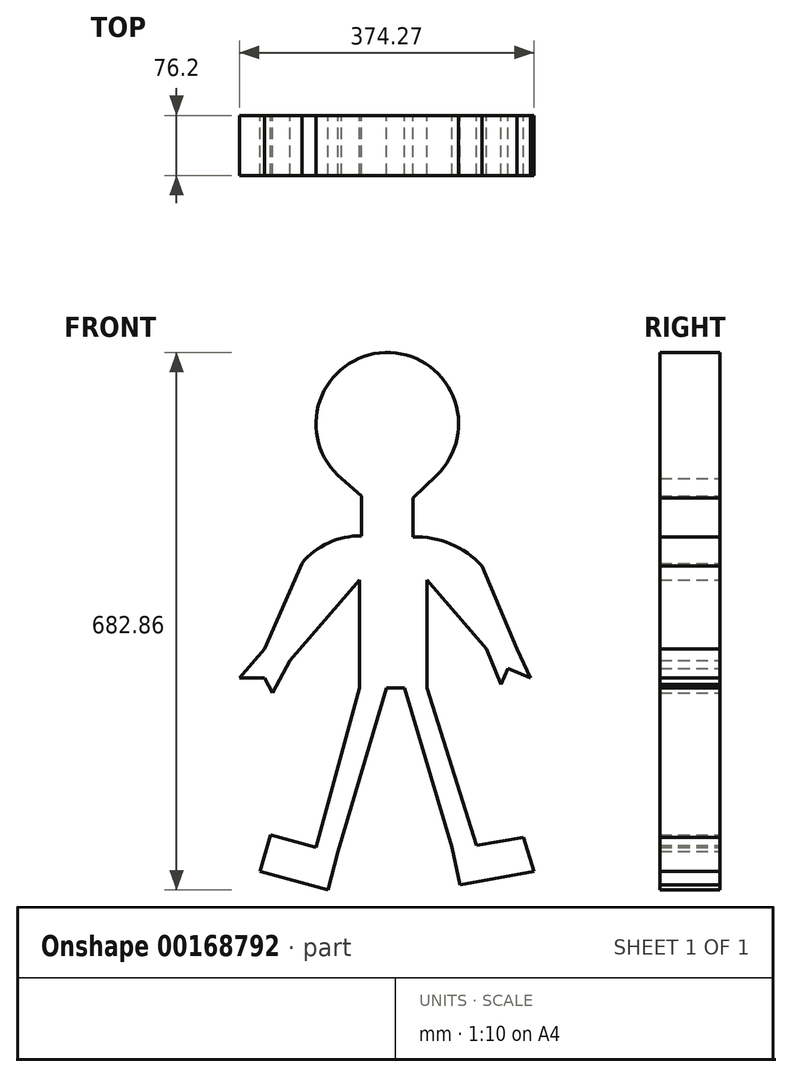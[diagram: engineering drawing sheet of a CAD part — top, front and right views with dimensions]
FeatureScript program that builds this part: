
annotation { "Feature Type Name" : "Feature", "Feature Type Description" : "" }
export const myFeature = defineFeature(function(context is Context, id is Id, definition is map)
    precondition{}
    {
        {
            var Q0;
            Q0=qCreatedBy(makeId("Front.planeOp"),FACE);
            var sketch = newSketch(context, id + "F0", { "sketchPlane" : qUnion([Q0])});
            skLineSegment(sketch, "E0", {"start": v(-65.27, 231.14) * mm, "end": v(-65.27, 180.67) * mm});
            skLineSegment(sketch, "E1", {"start": v(0, 228.8) * mm, "end": v(0, 179.25) * mm});
            skCircle(sketch, "E2", {"center": v(-32.54, 323) * mm, "radius": 90.58 * mm});
            skArc(sketch, "E3", {"start": v(-65.27, 180.67) * mm, "mid": v(-107.07, 171.83) * mm, "end": v(-140.92, 145.77) * mm});
            skArc(sketch, "E4", {"start": v(87.57, 142.42) * mm, "mid": v(47.85, 170.5) * mm, "end": v(0, 179.25) * mm});
            skLineSegment(sketch, "E5", {"start": v(-140.92, 145.77) * mm, "end": v(-188.63, 36.96) * mm});
            skLineSegment(sketch, "E6", {"start": v(-188.63, 36.96) * mm, "end": v(-155.84, 22.59) * mm});
            skLineSegment(sketch, "E7", {"start": v(-155.84, 22.59) * mm, "end": v(-68.1, 124.84) * mm});
            skLineSegment(sketch, "E8", {"start": v(-68.1, 124.84) * mm, "end": v(-68.1, -12.42) * mm});
            skLineSegment(sketch, "E9", {"start": v(-68.1, -12.42) * mm, "end": v(18.1, -12.42) * mm});
            skLineSegment(sketch, "E10", {"start": v(18.1, -12.42) * mm, "end": v(18.1, 124.84) * mm});
            skLineSegment(sketch, "E11", {"start": v(18.1, 124.84) * mm, "end": v(93.49, 36.96) * mm});
            skLineSegment(sketch, "E12", {"start": v(93.49, 36.96) * mm, "end": v(131.93, 36.96) * mm});
            skLineSegment(sketch, "E13", {"start": v(131.93, 36.96) * mm, "end": v(87.57, 142.42) * mm});
            skLineSegment(sketch, "E14", {"start": v(-68.1, -12.42) * mm, "end": v(-123.35, -214.96) * mm});
            skLineSegment(sketch, "E15", {"start": v(-33.79, -12.42) * mm, "end": v(-94.89, -219.99) * mm});
            skLineSegment(sketch, "E16", {"start": v(-10.35, -12.42) * mm, "end": v(49.9, -214.96) * mm});
            skLineSegment(sketch, "E17", {"start": v(18.1, -12.42) * mm, "end": v(80.87, -212.45) * mm});
            skLineSegment(sketch, "E18", {"start": v(80.87, -212.45) * mm, "end": v(140.3, -202.41) * mm});
            skLineSegment(sketch, "E19", {"start": v(140.3, -202.41) * mm, "end": v(153.93, -245.86) * mm});
            skLineSegment(sketch, "E20", {"start": v(153.93, -245.86) * mm, "end": v(59.95, -262.67) * mm});
            skLineSegment(sketch, "E21", {"start": v(59.95, -262.67) * mm, "end": v(49.9, -214.96) * mm});
            skLineSegment(sketch, "E22", {"start": v(-123.35, -214.96) * mm, "end": v(-181.13, -199.2) * mm});
            skLineSegment(sketch, "E23", {"start": v(-181.13, -199.2) * mm, "end": v(-193.86, -245.86) * mm});
            skLineSegment(sketch, "E24", {"start": v(-193.86, -245.86) * mm, "end": v(-107.95, -269.28) * mm});
            skLineSegment(sketch, "E25", {"start": v(-107.95, -269.28) * mm, "end": v(-94.89, -219.99) * mm});
            skLineSegment(sketch, "E26", {"start": v(-188.63, 36.96) * mm, "end": v(-220.34, 0) * mm});
            skLineSegment(sketch, "E27", {"start": v(-220.34, 0) * mm, "end": v(-188.63, 0) * mm});
            skLineSegment(sketch, "E28", {"start": v(-188.63, 0) * mm, "end": v(-178.4, -19.02) * mm});
            skLineSegment(sketch, "E29", {"start": v(-178.4, -19.02) * mm, "end": v(-155.84, 22.59) * mm});
            skLineSegment(sketch, "E30", {"start": v(93.49, 36.96) * mm, "end": v(111.65, -8.12) * mm});
            skLineSegment(sketch, "E31", {"start": v(111.65, -8.12) * mm, "end": v(120.67, 12.45) * mm});
            skLineSegment(sketch, "E32", {"start": v(120.67, 12.45) * mm, "end": v(149.07, 0) * mm});
            skLineSegment(sketch, "E33", {"start": v(149.07, 0) * mm, "end": v(131.93, 36.96) * mm});
            skLineSegment(sketch, "E34", {"start": v(-90.49, 253.38) * mm, "end": v(-65.27, 231.14) * mm});
            skLineSegment(sketch, "E35", {"start": v(0, 228.8) * mm, "end": v(30.05, 257.52) * mm});
            skSolve(sketch);
        }
        {
            var Q0;
            Q0 = qSketchRegion(id + "F0", true);
            extrude(context, id + "F1", {"entities" : qUnion([Q0]), "depth" : 76.2 * mm});
        }
    });
